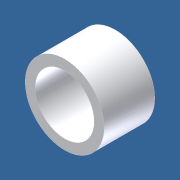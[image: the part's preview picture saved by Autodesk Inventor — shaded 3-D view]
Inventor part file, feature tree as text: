
AUTODESK INVENTOR PART (.ipt)
format: ipt  version: unknown  size: 167,936 bytes
history: native  units: in
note: dims shown in document units (in); Inventor stores cm internally (conversion verified against a paired STEP export)
features: extrude x1, sketch x1
ambient origin geometry x8: Origin, YZ Plane, XZ Plane, XY Plane, X Axis, Y Axis, Z Axis, Center Point
bodies: Solid1 (feature_tree)
feature tree (2):
  extrude  "Extrusion1"  Depth=0.5in
  sketch  "Sketch1"  dims[d0=0.375in d1=0.5in d2=0.3213in d3=0.0in]
